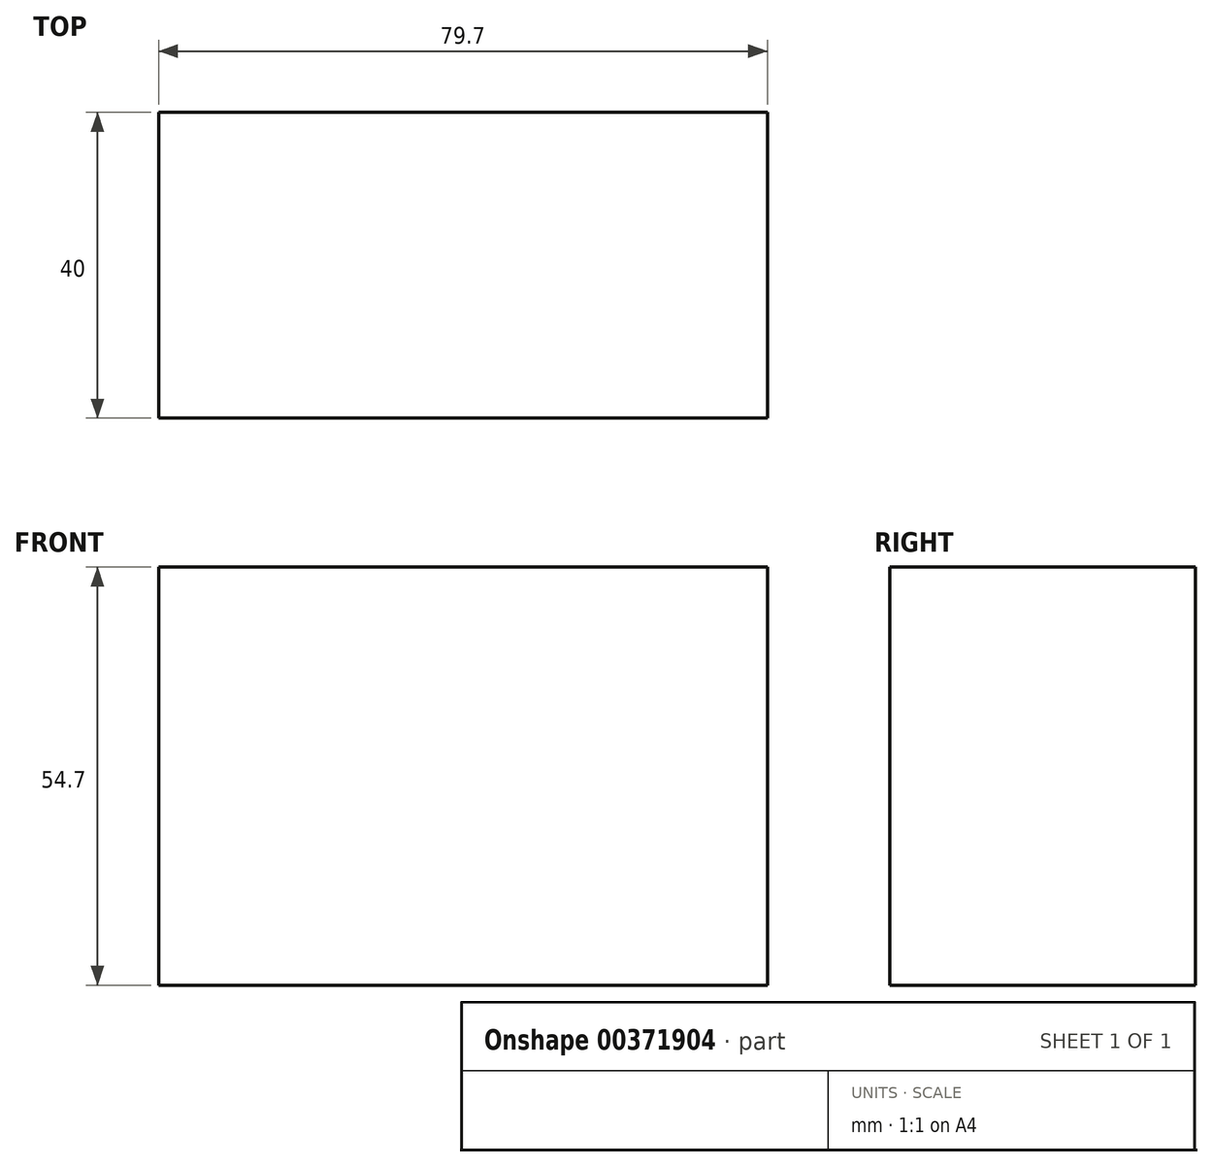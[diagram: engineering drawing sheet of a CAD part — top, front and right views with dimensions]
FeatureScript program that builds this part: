
annotation { "Feature Type Name" : "Feature", "Feature Type Description" : "" }
export const myFeature = defineFeature(function(context is Context, id is Id, definition is map)
    precondition{}
    {
        {
            var Q0;
            Q0=qCreatedBy(makeId("Front.planeOp"),FACE);
            var sketch = newSketch(context, id + "F0", { "sketchPlane" : qUnion([Q0])});
            skLineSegment(sketch, "E0.bottom", {"start": v(35, -22.5) * mm, "end": v(-35, -22.5) * mm, "construction": true});
            skLineSegment(sketch, "E0.top", {"start": v(35, 22.5) * mm, "end": v(-35, 22.5) * mm, "construction": true});
            skLineSegment(sketch, "E0.left", {"start": v(35, -22.5) * mm, "end": v(35, 22.5) * mm, "construction": true});
            skLineSegment(sketch, "E0.right", {"start": v(-35, -22.5) * mm, "end": v(-35, 22.5) * mm, "construction": true});
            skPoint(sketch, "E0.middle", {"position": v(0, 0) * mm});
            skLineSegment(sketch, "E1.bottom", {"start": v(39.85, 27.35) * mm, "end": v(-39.85, 27.35) * mm});
            skLineSegment(sketch, "E1.top", {"start": v(39.85, -27.35) * mm, "end": v(-39.85, -27.35) * mm});
            skLineSegment(sketch, "E1.left", {"start": v(39.85, 27.35) * mm, "end": v(39.85, -27.35) * mm});
            skLineSegment(sketch, "E1.right", {"start": v(-39.85, 27.35) * mm, "end": v(-39.85, -27.35) * mm});
            skSolve(sketch);
        }
        {
            var Q0;
            Q0 = qSketchRegion(id + "F0", true);
            extrude(context, id + "F1", {"entities" : qUnion([Q0]), "oppositeDirection" : true, "depth" : 40 * mm});
        }
    });
